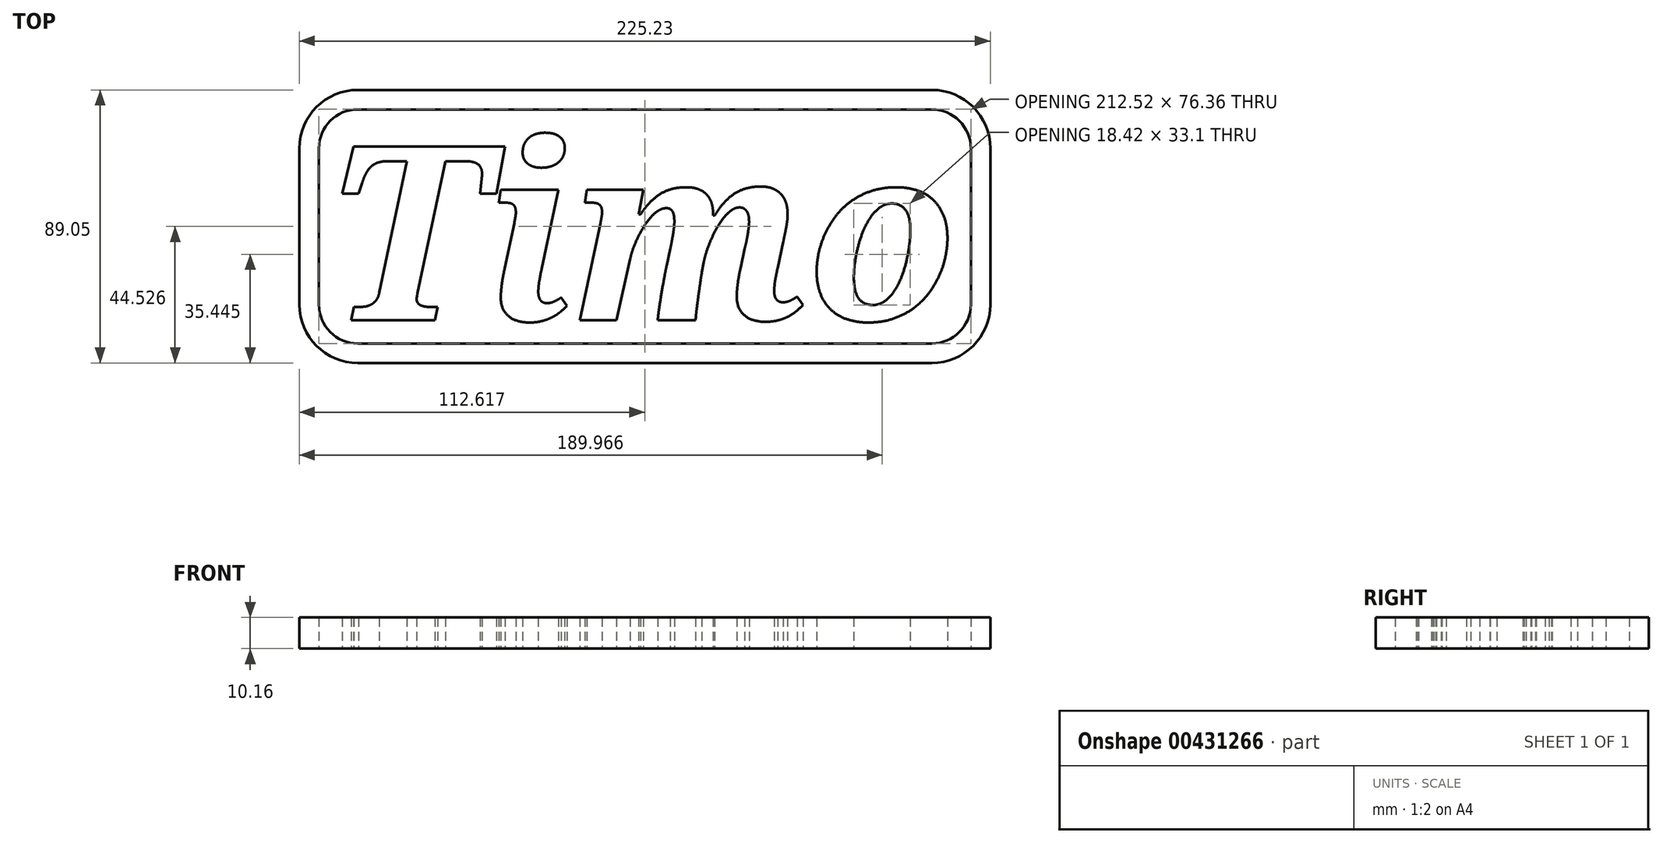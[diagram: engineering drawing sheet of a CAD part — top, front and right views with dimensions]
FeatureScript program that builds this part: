
annotation { "Feature Type Name" : "Feature", "Feature Type Description" : "" }
export const myFeature = defineFeature(function(context is Context, id is Id, definition is map)
    precondition{}
    {
        {
            var Q0;
            Q0=qCreatedBy(makeId("Top.planeOp"),FACE);
            var sketch = newSketch(context, id + "F0", { "sketchPlane" : qUnion([Q0])});
            skText(sketch, "E0", { "text": "Timo", "fontName": "NotoSerif-BoldItalic.ttf"});
            const initialGuessF0  = {"E0": [-0.099, 0.00508, 1, 0, 0.05715]};
            skSetInitialGuess(sketch, initialGuessF0);
            skSolve(sketch);
        }
        {
            var Q0;
            Q0 = qSketchRegion(id + "F0", true);
            extrude(context, id + "F1", {"entities" : qUnion([Q0]), "depth" : 10.16 * mm});
        }
        {
            var Q0;
            Q0=qCreatedBy(makeId("Top.planeOp"),FACE);
            var sketch = newSketch(context, id + "F2", { "sketchPlane" : qUnion([Q0])});
            skLineSegment(sketch, "E1.bottom", {"start": v(-88.55, 73.81) * mm, "end": v(98.58, 73.81) * mm});
            skLineSegment(sketch, "E1.top", {"start": v(-88.55, -2.54) * mm, "end": v(98.58, -2.54) * mm});
            skLineSegment(sketch, "E1.left", {"start": v(-101.25, 61.11) * mm, "end": v(-101.25, 10.16) * mm});
            skLineSegment(sketch, "E1.right", {"start": v(111.28, 61.11) * mm, "end": v(111.28, 10.16) * mm});
            skPoint(sketch, "E2.visualSharp", {"position": v(-101.25, 73.81) * mm});
            skArc(sketch, "E2.filletArc", {"start": v(-88.55, 73.81) * mm, "mid": v(-97.53, 70.1) * mm, "end": v(-101.25, 61.11) * mm});
            skPoint(sketch, "E3.visualSharp", {"position": v(111.28, 73.81) * mm});
            skArc(sketch, "E3.filletArc", {"start": v(111.28, 61.11) * mm, "mid": v(107.56, 70.1) * mm, "end": v(98.58, 73.81) * mm});
            skPoint(sketch, "E4.visualSharp", {"position": v(111.28, -2.54) * mm});
            skArc(sketch, "E4.filletArc", {"start": v(98.58, -2.54) * mm, "mid": v(107.56, 1.18) * mm, "end": v(111.28, 10.16) * mm});
            skPoint(sketch, "E5.visualSharp", {"position": v(-101.25, -2.54) * mm});
            skArc(sketch, "E5.filletArc", {"start": v(-101.25, 10.16) * mm, "mid": v(-97.53, 1.18) * mm, "end": v(-88.55, -2.54) * mm});
            skLineSegment(sketch, "E6.0", {"start": v(-88.55, 80.16) * mm, "end": v(98.58, 80.16) * mm});
            skLineSegment(sketch, "E6.1", {"start": v(-88.55, -8.9) * mm, "end": v(98.58, -8.9) * mm});
            skArc(sketch, "E6.2", {"start": v(-107.6, 10.16) * mm, "mid": v(-102.02, -3.31) * mm, "end": v(-88.55, -8.9) * mm});
            skLineSegment(sketch, "E6.3", {"start": v(-107.6, 61.11) * mm, "end": v(-107.6, 10.16) * mm});
            skArc(sketch, "E6.4", {"start": v(-88.55, 80.16) * mm, "mid": v(-102.02, 74.59) * mm, "end": v(-107.6, 61.11) * mm});
            skArc(sketch, "E7.0", {"start": v(117.63, 61.11) * mm, "mid": v(112.05, 74.59) * mm, "end": v(98.58, 80.16) * mm});
            skLineSegment(sketch, "E7.1", {"start": v(117.63, 61.11) * mm, "end": v(117.63, 10.16) * mm});
            skArc(sketch, "E7.2", {"start": v(98.58, -8.9) * mm, "mid": v(112.05, -3.31) * mm, "end": v(117.63, 10.16) * mm});
            skSolve(sketch);
        }
        {
            var Q0;
            Q0 = qSketchRegion(id + "F2", true);
            extrude(context, id + "F3", {"entities" : qUnion([Q0]), "depth" : 10.16 * mm});
        }
    });
